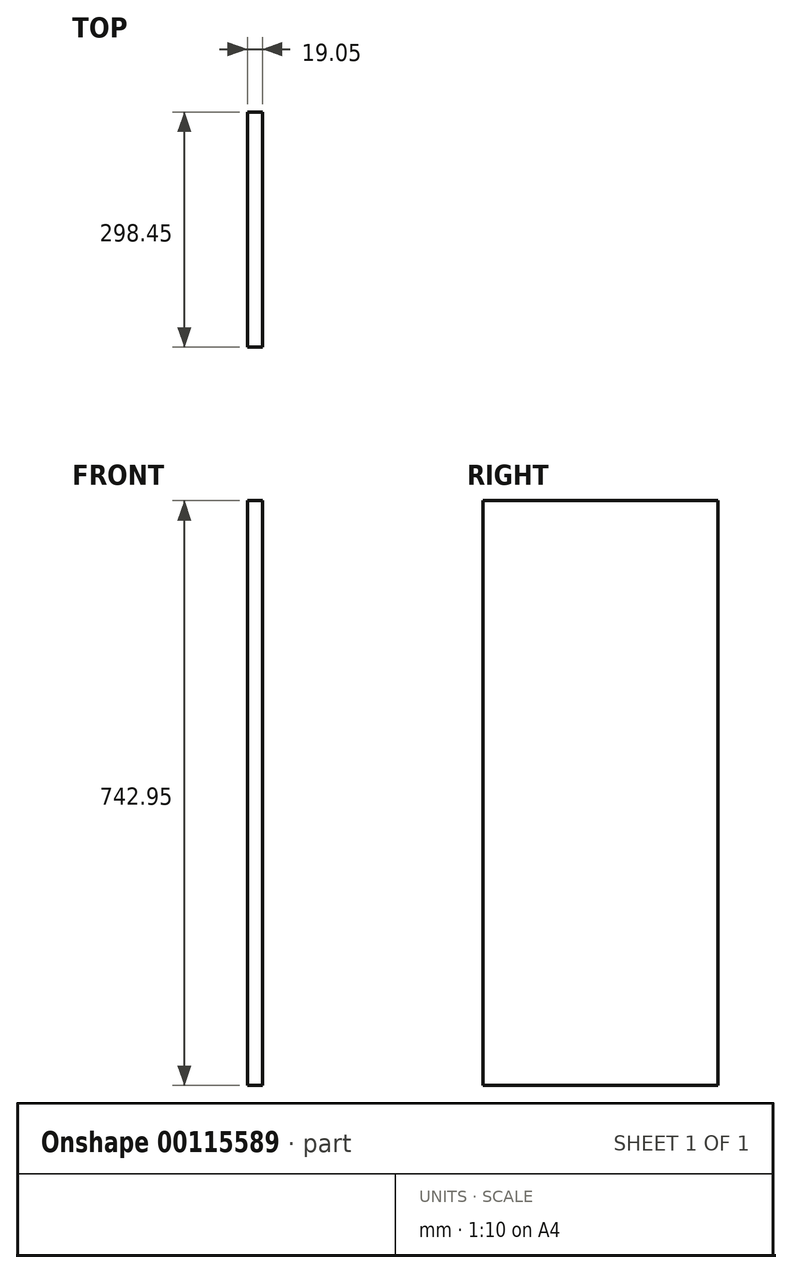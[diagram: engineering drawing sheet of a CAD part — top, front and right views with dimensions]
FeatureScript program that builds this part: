
annotation { "Feature Type Name" : "Feature", "Feature Type Description" : "" }
export const myFeature = defineFeature(function(context is Context, id is Id, definition is map)
    precondition{}
    {
        {
            var Q0;
            Q0=qCreatedBy(makeId("Right.planeOp"),FACE);
            var sketch = newSketch(context, id + "F0", { "sketchPlane" : qUnion([Q0])});
            skLineSegment(sketch, "E0.bottom", {"start": v(0, 0) * mm, "end": v(298.45, 0) * mm});
            skLineSegment(sketch, "E0.top", {"start": v(0, 742.95) * mm, "end": v(298.45, 742.95) * mm});
            skLineSegment(sketch, "E0.left", {"start": v(0, 0) * mm, "end": v(0, 742.95) * mm});
            skLineSegment(sketch, "E0.right", {"start": v(298.45, 0) * mm, "end": v(298.45, 742.95) * mm});
            skSolve(sketch);
        }
        {
            var Q0;
            Q0=makeQuery(id+"F0.imprint","IMPRINT",FACE,{"disambiguationData":[TD([[makeQuery(id+"F0.imprint","IMPRINT",EDGE,{"derivedFrom":sQuery(id+"F0.wireOp",EDGE,"E0.bottom")}),1.0]])]});
            extrude(context, id + "F1", {"entities" : qUnion([Q0]), "depth" : 19.05 * mm});
        }
    });
